# Revit family: Domotics-DomesticRanges-GEWISS-SYSTEM_SIGNALLING-LAMP_STAIR_RISER
name_source: partatom
category: Apparecchi elettrici
revit_build: Autodesk Revit 2016 (Build: 20161004_0715(x64)
units: mm (PartAtom-declared; Revit-internal decimal feet)

## family parameters
Condiviso = Sì
Host = Superficie
Mantenere orientamento annotazione = Sì
Punto di calcolo locali = Sì
Quota connettore circolare = Usa diametro
Taglio con vuoti quando caricato = No
Tipo di parte = Normale

## types (5) — shared parameters
Catalogue = DOMOTICS
Catalogue Range = SYSTEM - DOMESTIC RANGE
Description. = Stair riser lamp
Electrocod = 0132
Fixing for lamp = Cartridge
IDF = 27b20512-f0cd-4c6a-a13a-b587bbdd2201
IDT = fca23135-4530-4210-9352-b52efd479bc1
Immagine tipo = GW20626.jpg
Lamp holder = Cartridge
No. SYSTEM modules = 3
Produttore = GEWISS S.p.A.
Prospetto di default = 1219 mm
SEO = Lamp
Technical sheet = https://www.gewiss.com
Tipo_ = System Spie Segnapasso_GENERICO : GW20626 Spia segnapasso con diffusore piano azzurro
URL = https://www.gewiss.com
Version file RFA = 19.4
Voltage = 12/24V AC
Voltage: = 12/24V AC

## per-type parameters (varying)
| type | Descrizione | Diffuser colour | Diffuser colour: | EAN code | Modello |
| GW20601 - Stair riser diffuser flat lamp opal | STAIR RISER DIFFUSER FLAT LAMP OPAL | Opal | Opal | 8011564001053 | GW20601 |
| GW20623 - Stair riser diffuser flat lamp red | STAIR RISER DIFFUSER FLAT LAMP RED | Red | Red | 8011564024816 | GW20623 |
| GW20624 - Stair riser diffuser flat lamp green | STAIR RISER DIFFUSER FLAT LAMP GREEN | Green | Green | 8011564024809 | GW20624 |
| GW20625 - Stair riser diffuser flat lamp yellow | STAIR RISER DIFFUSER FLAT LAMP YELLOW | Yellow | Yellow | 8011564024793 | GW20625 |
| GW20626 - Stair riser diffuser flat lamp blue | STAIR RISER DIFFUSER FLAT LAMP BLUE | Light blue | Light blue | 8011564024786 | GW20626 |

## geometry (parser evidence)
native form markers: Sweep x1
no freeform markers — native parametric forms only
